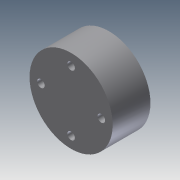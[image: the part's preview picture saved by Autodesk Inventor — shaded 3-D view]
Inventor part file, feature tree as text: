
AUTODESK INVENTOR PART (.ipt)
format: ipt  version: 2011 (Build 150239000, 239)  size: 88,064 bytes
history: native  units: in
note: dims shown in document units (in); Inventor stores cm internally (conversion verified against a paired STEP export)
features: extrude x2, sketch x2
ambient origin geometry x8: Origin, YZ Plane, XZ Plane, XY Plane, X Axis, Y Axis, Z Axis, Center Point
bodies: Solid1 (feature_tree)
feature tree (4):
  extrude  "Extrusion1"  Depth=0.3937in TaperAngle=0.0deg
  extrude  "Extrusion2"  Depth=0.0787in
  sketch  "Sketch1"  dims[d0=0.8661in d1=0.3937in d2=0.0in]
  sketch  "Sketch2"  dims[d3=0.6299in d4=0.0787in d5=0.0787in d6=0.0787in d7=0.0787in d8=0.3937in d9=0.0in]
